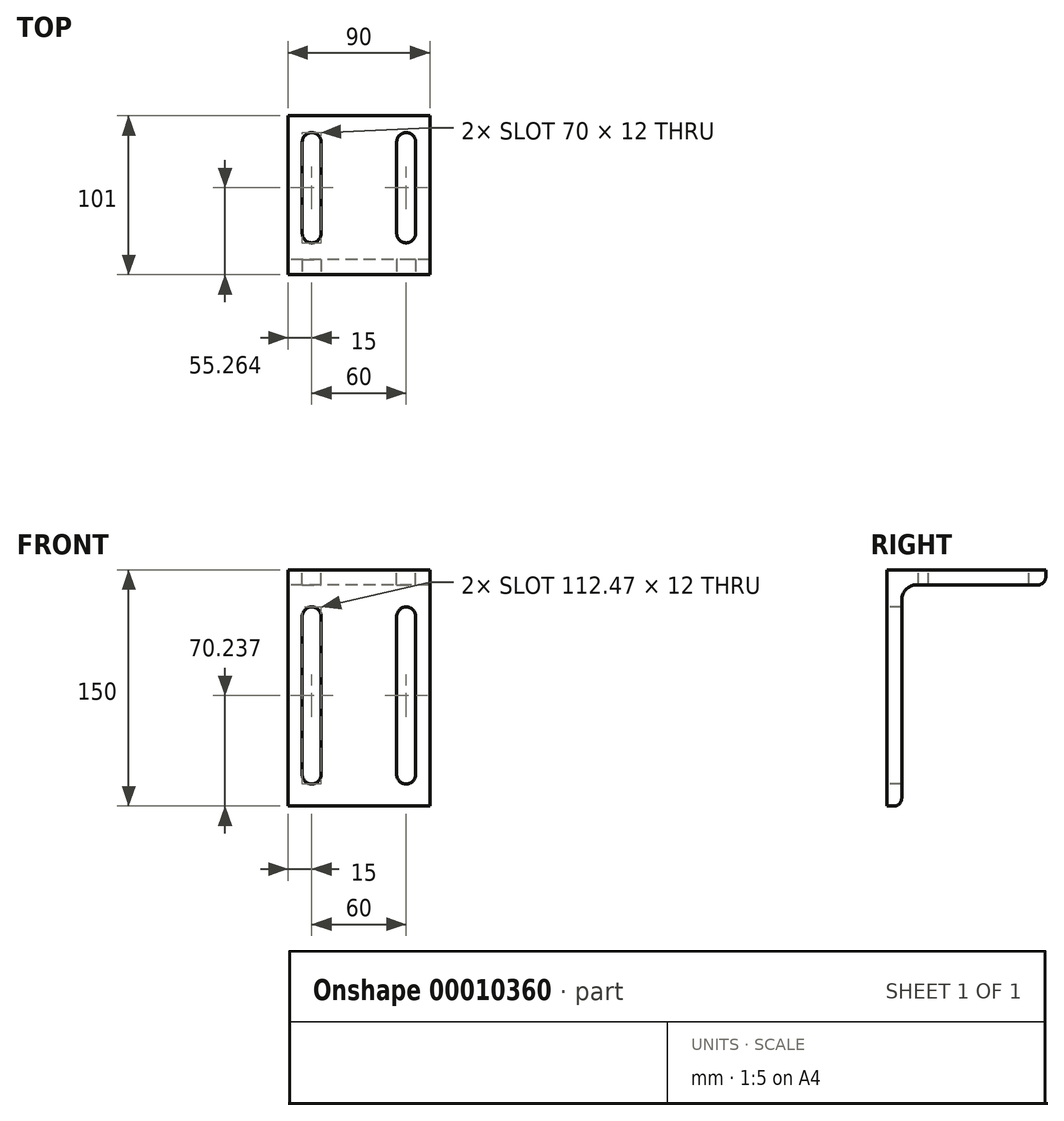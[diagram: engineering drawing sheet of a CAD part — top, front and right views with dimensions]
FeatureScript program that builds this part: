
annotation { "Feature Type Name" : "Feature", "Feature Type Description" : "" }
export const myFeature = defineFeature(function(context is Context, id is Id, definition is map)
    precondition{}
    {
        {
            var Q0;
            Q0=qCreatedBy(makeId("Right.planeOp"),FACE);
            var sketch = newSketch(context, id + "F0", { "sketchPlane" : qUnion([Q0])});
            skLineSegment(sketch, "E0.bottom", {"start": v(0, 0) * mm, "end": v(101, 0) * mm});
            skLineSegment(sketch, "E0.top", {"start": v(0, -150) * mm, "end": v(9.53, -150) * mm});
            skLineSegment(sketch, "E0.left", {"start": v(0, 0) * mm, "end": v(0, -150) * mm});
            skLineSegment(sketch, "E0.right", {"start": v(101, 0) * mm, "end": v(101, -9.52) * mm});
            skLineSegment(sketch, "E1.0", {"start": v(19.05, -9.53) * mm, "end": v(101, -9.53) * mm});
            skLineSegment(sketch, "E1.1", {"start": v(9.53, -19.05) * mm, "end": v(9.53, -150) * mm});
            skPoint(sketch, "E2.visualSharp", {"position": v(9.52, -9.53) * mm});
            skArc(sketch, "E2.filletArc", {"start": v(19.05, -9.53) * mm, "mid": v(12.31, -12.31) * mm, "end": v(9.53, -19.05) * mm});
            skSolve(sketch);
        }
        {
            var Q0;
            Q0 = qSketchRegion(id + "F0", true);
            extrude(context, id + "F1", {"entities" : qUnion([Q0]), "endBound" : BoundingType.SYMMETRIC, "depth" : 90 * mm});
        }
        {
            var Q0;
            Q0=makeQuery(id+"F1.opExtrude","SWEPT_FACE",FACE,{"disambiguationData":[OSD([sQuery(id+"F0.wireOp",EDGE,"E0.bottom")])]});
            var sketch = newSketch(context, id + "F2", { "sketchPlane" : qUnion([Q0])});
            skLineSegment(sketch, "E3", {"start": v(0, 0) * mm, "end": v(0, 101) * mm, "construction": true});
            skLineSegment(sketch, "E4.0", {"start": v(30, 9.52) * mm, "end": v(30, 101) * mm, "construction": true});
            skLineSegment(sketch, "E5.0", {"start": v(45, 9.53) * mm, "end": v(-45, 9.53) * mm, "construction": true});
            skLineSegment(sketch, "E6", {"start": v(30, 55.26) * mm, "end": v(-17.36, 55.26) * mm, "construction": true});
            skLineSegment(sketch, "E7.0", {"start": v(30, 26.26) * mm, "end": v(-17.36, 26.26) * mm, "construction": true});
            skArc(sketch, "E8", {"start": v(24, 26.26) * mm, "mid": v(30.17, 20.26) * mm, "end": v(36, 26.6) * mm});
            skArc(sketch, "E9.0.MirrorC", {"start": v(24, 84.26) * mm, "mid": v(30, 90.26) * mm, "end": v(36, 84.26) * mm});
            skLineSegment(sketch, "E10", {"start": v(24, 26.26) * mm, "end": v(24, 84.26) * mm});
            skLineSegment(sketch, "E11", {"start": v(36, 26.6) * mm, "end": v(36, 84.26) * mm});
            skLineSegment(sketch, "E12.0.MirrorCS", {"start": v(-24, 26.26) * mm, "end": v(-24, 84.26) * mm});
            skLineSegment(sketch, "E12.1.MirrorCS", {"start": v(-36, 26.6) * mm, "end": v(-36, 84.26) * mm});
            skArc(sketch, "E12.2.MirrorCS", {"start": v(-24, 26.26) * mm, "mid": v(-30.17, 20.26) * mm, "end": v(-36, 26.6) * mm});
            skArc(sketch, "E12.3.MirrorCS", {"start": v(-24, 84.26) * mm, "mid": v(-30, 90.26) * mm, "end": v(-36, 84.26) * mm});
            skSolve(sketch);
        }
        {
            var Q0;
            Q0 = qSketchRegion(id + "F2", true);
            extrude(context, id + "F3", {"entities" : qUnion([Q0]), "operationType" : NewBodyOperationType.REMOVE, "endBound" : BoundingType.THROUGH_ALL, "oppositeDirection" : true, "depth" : 25 * mm});
        }
        {
            var Q0;
            Q0=makeQuery(id+"F1.opExtrude","SWEPT_EDGE",EDGE,{"disambiguationData":[OSD([sQuery(id+"F0.wireOp",EDGE,"E0.right"),sQuery(id+"F0.wireOp",EDGE,"E1.0")])]});
            fillet(context, id + "F4", {"entities" : qUnion([Q0]), "radius" : 5 * mm, "tangentPropagation" : true, "allowEdgeOverflow" : false});
        }
        {
            var Q0;
            Q0=makeQuery(id+"F1.opExtrude","SWEPT_FACE",FACE,{"disambiguationData":[OSD([sQuery(id+"F0.wireOp",EDGE,"E0.left")])]});
            var sketch = newSketch(context, id + "F5", { "sketchPlane" : qUnion([Q0])});
            skLineSegment(sketch, "E13", {"start": v(0, 0) * mm, "end": v(0, -160) * mm, "construction": true});
            skLineSegment(sketch, "E14.0", {"start": v(45, -29.53) * mm, "end": v(-45, -29.53) * mm, "construction": true});
            skLineSegment(sketch, "E15.0", {"start": v(45, -130) * mm, "end": v(-45, -130) * mm, "construction": true});
            skLineSegment(sketch, "E16.0", {"start": v(-30, 0) * mm, "end": v(-30, -160) * mm, "construction": true});
            skArc(sketch, "E17", {"start": v(-36, -130) * mm, "mid": v(-30, -136) * mm, "end": v(-24, -130) * mm});
            skArc(sketch, "E18", {"start": v(-24, -29.53) * mm, "mid": v(-30, -23.53) * mm, "end": v(-36, -29.53) * mm});
            skLineSegment(sketch, "E19", {"start": v(-36, -29.53) * mm, "end": v(-36, -130) * mm});
            skLineSegment(sketch, "E20", {"start": v(-24, -29.53) * mm, "end": v(-24, -130) * mm});
            skLineSegment(sketch, "E21.0.MirrorCS", {"start": v(36, -29.53) * mm, "end": v(36, -130) * mm});
            skArc(sketch, "E21.1.MirrorCS", {"start": v(36, -130) * mm, "mid": v(30, -136) * mm, "end": v(24, -130) * mm});
            skLineSegment(sketch, "E21.2.MirrorCS", {"start": v(24, -29.53) * mm, "end": v(24, -130) * mm});
            skArc(sketch, "E21.3.MirrorCS", {"start": v(24, -29.53) * mm, "mid": v(30, -23.53) * mm, "end": v(36, -29.53) * mm});
            skSolve(sketch);
        }
        {
            var Q0;
            Q0 = qSketchRegion(id + "F5", true);
            extrude(context, id + "F6", {"entities" : qUnion([Q0]), "operationType" : NewBodyOperationType.REMOVE, "endBound" : BoundingType.THROUGH_ALL, "oppositeDirection" : true, "depth" : 25 * mm});
        }
        {
            var Q0;
            Q0=makeQuery(id+"F1.opExtrude","SWEPT_EDGE",EDGE,{"disambiguationData":[OSD([sQuery(id+"F0.wireOp",EDGE,"E0.top"),sQuery(id+"F0.wireOp",EDGE,"E1.1")])]});
            fillet(context, id + "F7", {"entities" : qUnion([Q0]), "radius" : 5 * mm, "tangentPropagation" : true, "allowEdgeOverflow" : false});
        }
    });
